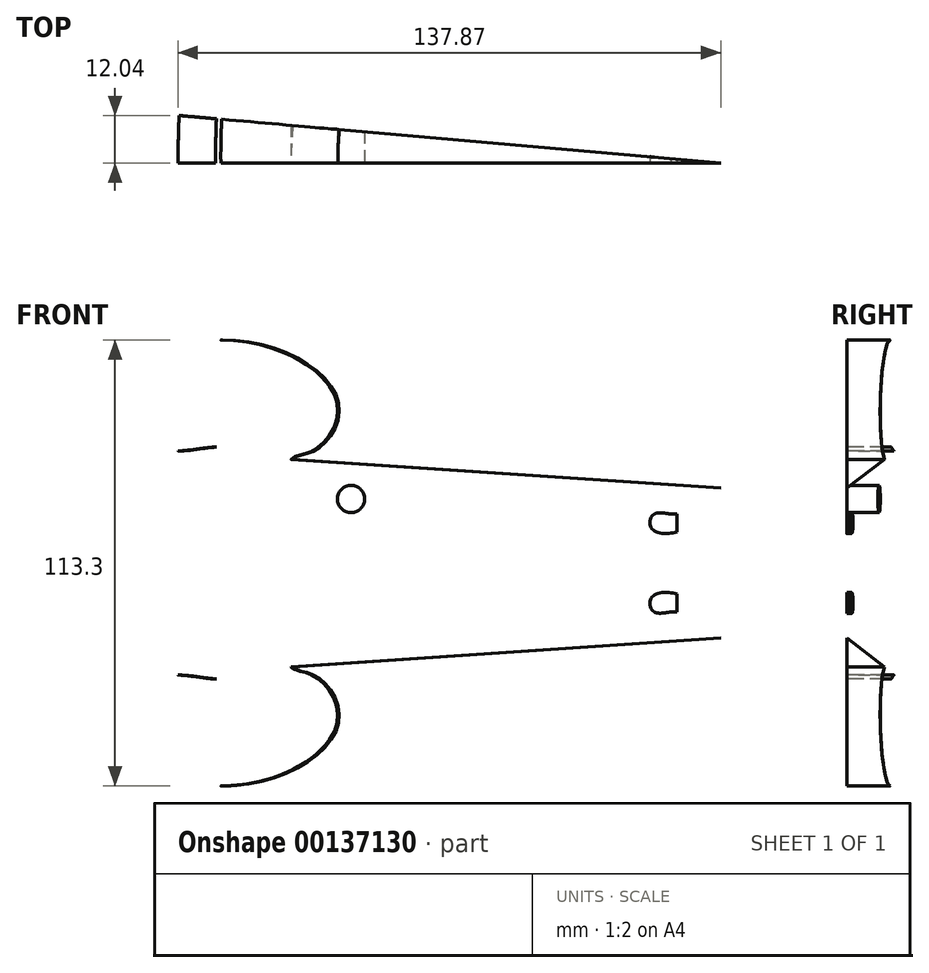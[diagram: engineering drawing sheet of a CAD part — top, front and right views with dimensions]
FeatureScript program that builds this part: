
annotation { "Feature Type Name" : "Feature", "Feature Type Description" : "" }
export const myFeature = defineFeature(function(context is Context, id is Id, definition is map)
    precondition{}
    {
        {
            var Q0;
            Q0=qCreatedBy(makeId("Front.planeOp"),FACE);
            var sketch = newSketch(context, id + "F0", { "sketchPlane" : qUnion([Q0])});
            skLineSegment(sketch, "E0", {"start": v(-58.83, 0) * mm, "end": v(56.17, 0) * mm});
            skCircle(sketch, "E1", {"center": v(-58.83, 0) * mm, "radius": 27 * mm});
            skLineSegment(sketch, "E2", {"start": v(56.17, -19) * mm, "end": v(-53, -26.36) * mm});
            skFitSpline(sketch, "E3", {"points": [v(-53, -26.36) * mm, v(-47.32, -28.61) * mm, v(-41.14, -39.33) * mm, v(-55.31, -53.68) * mm, v(-83.47, -53.86) * mm, v(-90.92, -40.06) * mm, v(-84.38, -28.8) * mm, v(-69.48, -28.8) * mm, v(-66.21, -19.9) * mm, v(-56.58, -19.35) * mm, v(-53, -26.36) * mm]});
            skLineSegment(sketch, "E4.MirrorCS", {"start": v(56.17, 19) * mm, "end": v(-53, 26.36) * mm});
            skFitSpline(sketch, "E5.MirrorC", {"points": [v(-53, 26.36) * mm, v(-47.32, 28.61) * mm, v(-41.14, 39.33) * mm, v(-55.31, 53.68) * mm, v(-83.47, 53.86) * mm, v(-90.92, 40.06) * mm, v(-84.38, 28.8) * mm, v(-69.48, 28.8) * mm, v(-66.21, 19.9) * mm, v(-56.58, 19.35) * mm, v(-53, 26.36) * mm]});
            skLineSegment(sketch, "E6", {"start": v(56.17, 19) * mm, "end": v(56.17, -19) * mm});
            skSolve(sketch);
        }
        {
            var Q0;
            {var subQ1=sQuery(id+"F0.wireOp",EDGE,"E1");var subQ4=sQuery(id+"F0.wireOp",EDGE,"E5.MirrorC");var subQ7=makeQuery(id+"F0.imprint","INTERSECT",VERTEX,{"derivedFrom":[subQ1,subQ4]});Q0=makeQuery(id+"F0.imprint","IMPRINT",FACE,{"disambiguationData":[TD([[makeQuery(id+"F0.imprint","IMPRINT",EDGE,{"disambiguationData":[TD([[subQ7,-1.0]])],"derivedFrom":subQ1}),1.0]])]});}
            var Q1;
            {var subQ0=sQuery(id+"F0.wireOp",EDGE,"E5.MirrorC");var subQ1=sQuery(id+"F0.wireOp",EDGE,"E1");var subQ3=makeQuery(id+"F0.imprint","INTERSECT",VERTEX,{"derivedFrom":[subQ1,subQ0]});Q1=makeQuery(id+"F0.imprint","IMPRINT",FACE,{"disambiguationData":[TD([[makeQuery(id+"F0.imprint","IMPRINT",EDGE,{"disambiguationData":[TD([[subQ3,1.0]])],"derivedFrom":subQ1}),1.0]])]});}
            var Q2;
            {var subQ0=sQuery(id+"F0.wireOp",EDGE,"E5.MirrorC");var subQ1=sQuery(id+"F0.wireOp",EDGE,"E1");var subQ3=makeQuery(id+"F0.imprint","INTERSECT",VERTEX,{"derivedFrom":[subQ1,subQ0]});Q2=makeQuery(id+"F0.imprint","IMPRINT",FACE,{"disambiguationData":[TD([[makeQuery(id+"F0.imprint","IMPRINT",EDGE,{"disambiguationData":[TD([[subQ3,1.0]])],"derivedFrom":subQ1}),-1.0]])]});}
            var Q3;
            {var subQ0=sQuery(id+"F0.wireOp",EDGE,"E3");var subQ1=sQuery(id+"F0.wireOp",EDGE,"E1");var subQ3=makeQuery(id+"F0.imprint","INTERSECT",VERTEX,{"derivedFrom":[subQ1,subQ0]});Q3=makeQuery(id+"F0.imprint","IMPRINT",FACE,{"disambiguationData":[TD([[makeQuery(id+"F0.imprint","IMPRINT",EDGE,{"disambiguationData":[TD([[subQ3,-1.0]])],"derivedFrom":subQ1}),1.0]])]});}
            var Q4;
            {var subQ0=sQuery(id+"F0.wireOp",EDGE,"E3");var subQ1=sQuery(id+"F0.wireOp",EDGE,"E1");var subQ3=makeQuery(id+"F0.imprint","INTERSECT",VERTEX,{"derivedFrom":[subQ1,subQ0]});Q4=makeQuery(id+"F0.imprint","IMPRINT",FACE,{"disambiguationData":[TD([[makeQuery(id+"F0.imprint","IMPRINT",EDGE,{"disambiguationData":[TD([[subQ3,-1.0]])],"derivedFrom":subQ1}),-1.0]])]});}
            var Q5;
            {var subQ5=sQuery(id+"F0.wireOp",EDGE,"E2");Q5=makeQuery(id+"F0.imprint","IMPRINT",FACE,{"disambiguationData":[TD([[makeQuery(id+"F0.imprint","IMPRINT",EDGE,{"derivedFrom":subQ5}),-1.0]])]});}
            var Q6;
            {var subQ5=sQuery(id+"F0.wireOp",EDGE,"E4.MirrorCS");Q6=makeQuery(id+"F0.imprint","IMPRINT",FACE,{"disambiguationData":[TD([[makeQuery(id+"F0.imprint","IMPRINT",EDGE,{"derivedFrom":subQ5}),1.0]])]});}
            var Q7;
            Q7=sQuery(id+"F0.wireOp",EDGE,"E6");
            revolve(context, id + "F1", {"entities" : qUnion([Q0, Q1, Q2, Q3, Q4, Q5, Q6]), "axis" : qUnion([Q7]), "revolveType" : RevolveType.ONE_DIRECTION, "angle" : 5 * degree});
        }
        {
            var Q0;
            Q0=makeQuery(id+"F1.opRevolve","CAP_FACE",FACE,{"disambiguationData":[OSD([sQuery(id+"F0.wireOp",EDGE,"E1"),sQuery(id+"F0.wireOp",EDGE,"E2"),sQuery(id+"F0.wireOp",EDGE,"E3"),sQuery(id+"F0.wireOp",EDGE,"E4.MirrorCS"),sQuery(id+"F0.wireOp",EDGE,"E5.MirrorC"),sQuery(id+"F0.wireOp",EDGE,"E6")])],"isStart":true});
            var sketch = newSketch(context, id + "F2", { "sketchPlane" : qUnion([Q0])});
            skCircle(sketch, "E7", {"center": v(-59.12, 0) * mm, "radius": 15 * mm});
            skLineSegment(sketch, "E8", {"start": v(-54.57, 14.3) * mm, "end": v(-3.41, 0) * mm});
            skLineSegment(sketch, "E9.MirrorCS", {"start": v(-54.57, -14.3) * mm, "end": v(-3.41, 0) * mm});
            skLineSegment(sketch, "E10.bottom", {"start": v(45.09, -12.44) * mm, "end": v(28.38, -12.44) * mm});
            skLineSegment(sketch, "E10.top", {"start": v(45.09, 12.44) * mm, "end": v(28.38, 12.44) * mm});
            skLineSegment(sketch, "E10.left", {"start": v(45.09, -12.44) * mm, "end": v(45.09, 12.44) * mm});
            skLineSegment(sketch, "E10.right", {"start": v(28.38, -12.44) * mm, "end": v(28.38, 12.44) * mm});
            skPoint(sketch, "E10.middle", {"position": v(36.73, 0) * mm});
            skFitSpline(sketch, "E11", {"points": [v(45.09, 12.44) * mm, v(47.81, 13.9) * mm, v(50.72, 12.44) * mm, v(51.08, 9.72) * mm, v(48.9, 9.36) * mm, v(45.09, 7.9) * mm, v(38.73, 8.63) * mm, v(39.28, 12.44) * mm, v(45.09, 12.44) * mm]});
            skFitSpline(sketch, "E12.MirrorC", {"points": [v(45.09, -12.44) * mm, v(47.81, -13.9) * mm, v(50.72, -12.44) * mm, v(51.08, -9.72) * mm, v(48.9, -9.36) * mm, v(45.09, -7.9) * mm, v(38.73, -8.63) * mm, v(39.28, -12.44) * mm, v(45.09, -12.44) * mm]});
            skFitSpline(sketch, "E13", {"points": [v(28.38, 12.44) * mm, v(8.4, 9.36) * mm, v(-16.31, 9.54) * mm, v(-33.03, 12.44) * mm, v(-38.84, 3.72) * mm, v(-37.02, -7.54) * mm, v(-28.48, -12.44) * mm, v(-2.14, -10.8) * mm, v(9.12, -9.9) * mm, v(28.38, -12.44) * mm, v(40.55, -4.09) * mm, v(34.37, 6.27) * mm, v(28.38, 12.44) * mm]});
            skCircle(sketch, "E14", {"center": v(-37.75, -16.26) * mm, "radius": 3.47 * mm});
            skCircle(sketch, "E15.MirrorC", {"center": v(-37.75, 16.26) * mm, "radius": 3.47 * mm});
            skSolve(sketch);
        }
        {
            var Q0;
            {var subQ0=sQuery(id+"F2.wireOp",EDGE,"E7");var subQ1=makeQuery(id+"F2.imprint","INTERSECT",VERTEX,{"derivedFrom":[subQ0,sQuery(id+"F2.wireOp",EDGE,"E8")]});Q0=makeQuery(id+"F2.imprint","IMPRINT",FACE,{"disambiguationData":[TD([[makeQuery(id+"F2.imprint","IMPRINT",EDGE,{"disambiguationData":[TD([[subQ1,-1.0]])],"derivedFrom":subQ0}),1.0]])]});}
            var Q1;
            {var subQ0=sQuery(id+"F2.wireOp",EDGE,"E8");var subQ1=sQuery(id+"F2.wireOp",EDGE,"E7");var subQ2=makeQuery(id+"F2.imprint","INTERSECT",VERTEX,{"derivedFrom":[subQ1,subQ0]});Q1=makeQuery(id+"F2.imprint","IMPRINT",FACE,{"disambiguationData":[TD([[makeQuery(id+"F2.imprint","IMPRINT",EDGE,{"disambiguationData":[TD([[subQ2,1.0]])],"derivedFrom":subQ1}),-1.0]])]});}
            var Q2;
            {var subQ0=sQuery(id+"F2.wireOp",EDGE,"E9.MirrorCS");var subQ1=sQuery(id+"F2.wireOp",EDGE,"E8");var subQ2=makeQuery(id+"F2.imprint","INTERSECT",VERTEX,{"derivedFrom":[subQ1,subQ0]});Q2=makeQuery(id+"F2.imprint","IMPRINT",FACE,{"disambiguationData":[TD([[makeQuery(id+"F2.imprint","IMPRINT",EDGE,{"disambiguationData":[TD([[subQ2,1.0]])],"derivedFrom":subQ1}),-1.0]])]});}
            var Q3;
            Q3=makeQuery(id+"F2.imprint","IMPRINT",FACE,{"disambiguationData":[TD([[makeQuery(id+"F2.imprint","IMPRINT",EDGE,{"derivedFrom":sQuery(id+"F2.wireOp",EDGE,"E15.MirrorC")}),-1.0]])]});
            var Q4;
            {var subQ0=sQuery(id+"F2.wireOp",EDGE,"E10.right");Q4=makeQuery(id+"F2.imprint","IMPRINT",FACE,{"disambiguationData":[TD([[makeQuery(id+"F2.imprint","IMPRINT",EDGE,{"derivedFrom":subQ0}),1.0]])]});}
            var Q5;
            Q5=makeQuery(id+"F2.imprint","IMPRINT",FACE,{"disambiguationData":[TD([[makeQuery(id+"F2.imprint","IMPRINT",EDGE,{"derivedFrom":sQuery(id+"F2.wireOp",EDGE,"E14")}),1.0]])]});
            var Q6;
            {var subQ0=sQuery(id+"F2.wireOp",EDGE,"E10.right");Q6=makeQuery(id+"F2.imprint","IMPRINT",FACE,{"disambiguationData":[TD([[makeQuery(id+"F2.imprint","IMPRINT",EDGE,{"derivedFrom":subQ0}),-1.0]])]});}
            var Q7;
            {var subQ3=sQuery(id+"F2.wireOp",EDGE,"E10.left");var subQ5=sQuery(id+"F2.wireOp",EDGE,"E12.MirrorC");var subQ6=makeQuery(id+"F2.imprint","INTERSECT",VERTEX,{"derivedFrom":[subQ3,subQ5]});Q7=makeQuery(id+"F2.imprint","IMPRINT",FACE,{"disambiguationData":[TD([[makeQuery(id+"F2.imprint","IMPRINT",EDGE,{"disambiguationData":[TD([[subQ6,-1.0]])],"derivedFrom":subQ3}),1.0]])]});}
            var Q8;
            {var subQ0=sQuery(id+"F2.wireOp",EDGE,"E11");var subQ1=sQuery(id+"F2.wireOp",EDGE,"E10.top");var subQ2=makeQuery(id+"F2.imprint","INTERSECT",VERTEX,{"disambiguationData":[OD(0.0)],"derivedFrom":[subQ1,subQ0]});Q8=makeQuery(id+"F2.imprint","IMPRINT",FACE,{"disambiguationData":[TD([[makeQuery(id+"F2.imprint","IMPRINT",EDGE,{"disambiguationData":[TD([[subQ2,-1.0]])],"derivedFrom":subQ1}),1.0]])]});}
            var Q9;
            {var subQ0=sQuery(id+"F2.wireOp",EDGE,"E11");var subQ1=sQuery(id+"F2.wireOp",EDGE,"E10.left");var subQ3=makeQuery(id+"F2.imprint","INTERSECT",VERTEX,{"derivedFrom":[subQ1,subQ0]});Q9=makeQuery(id+"F2.imprint","IMPRINT",FACE,{"disambiguationData":[TD([[makeQuery(id+"F2.imprint","IMPRINT",EDGE,{"disambiguationData":[TD([[subQ3,-1.0]])],"derivedFrom":subQ1}),-1.0]])]});}
            var Q10;
            {var subQ0=sQuery(id+"F2.wireOp",EDGE,"E12.MirrorC");var subQ1=sQuery(id+"F2.wireOp",EDGE,"E10.bottom");var subQ2=makeQuery(id+"F2.imprint","INTERSECT",VERTEX,{"disambiguationData":[OD(0.0)],"derivedFrom":[subQ1,subQ0]});Q10=makeQuery(id+"F2.imprint","IMPRINT",FACE,{"disambiguationData":[TD([[makeQuery(id+"F2.imprint","IMPRINT",EDGE,{"disambiguationData":[TD([[subQ2,-1.0]])],"derivedFrom":subQ1}),-1.0]])]});}
            var Q11;
            {var subQ0=sQuery(id+"F2.wireOp",EDGE,"E12.MirrorC");var subQ1=sQuery(id+"F2.wireOp",EDGE,"E10.left");var subQ3=makeQuery(id+"F2.imprint","INTERSECT",VERTEX,{"derivedFrom":[subQ1,subQ0]});Q11=makeQuery(id+"F2.imprint","IMPRINT",FACE,{"disambiguationData":[TD([[makeQuery(id+"F2.imprint","IMPRINT",EDGE,{"disambiguationData":[TD([[subQ3,1.0]])],"derivedFrom":subQ1}),-1.0]])]});}
            extrude(context, id + "F3", {"entities" : qUnion([Q0, Q1, Q2, Q3, Q4, Q5, Q6, Q7, Q8, Q9, Q10, Q11]), "operationType" : NewBodyOperationType.REMOVE, "oppositeDirection" : true, "depth" : 25 * mm});
        }
    });
